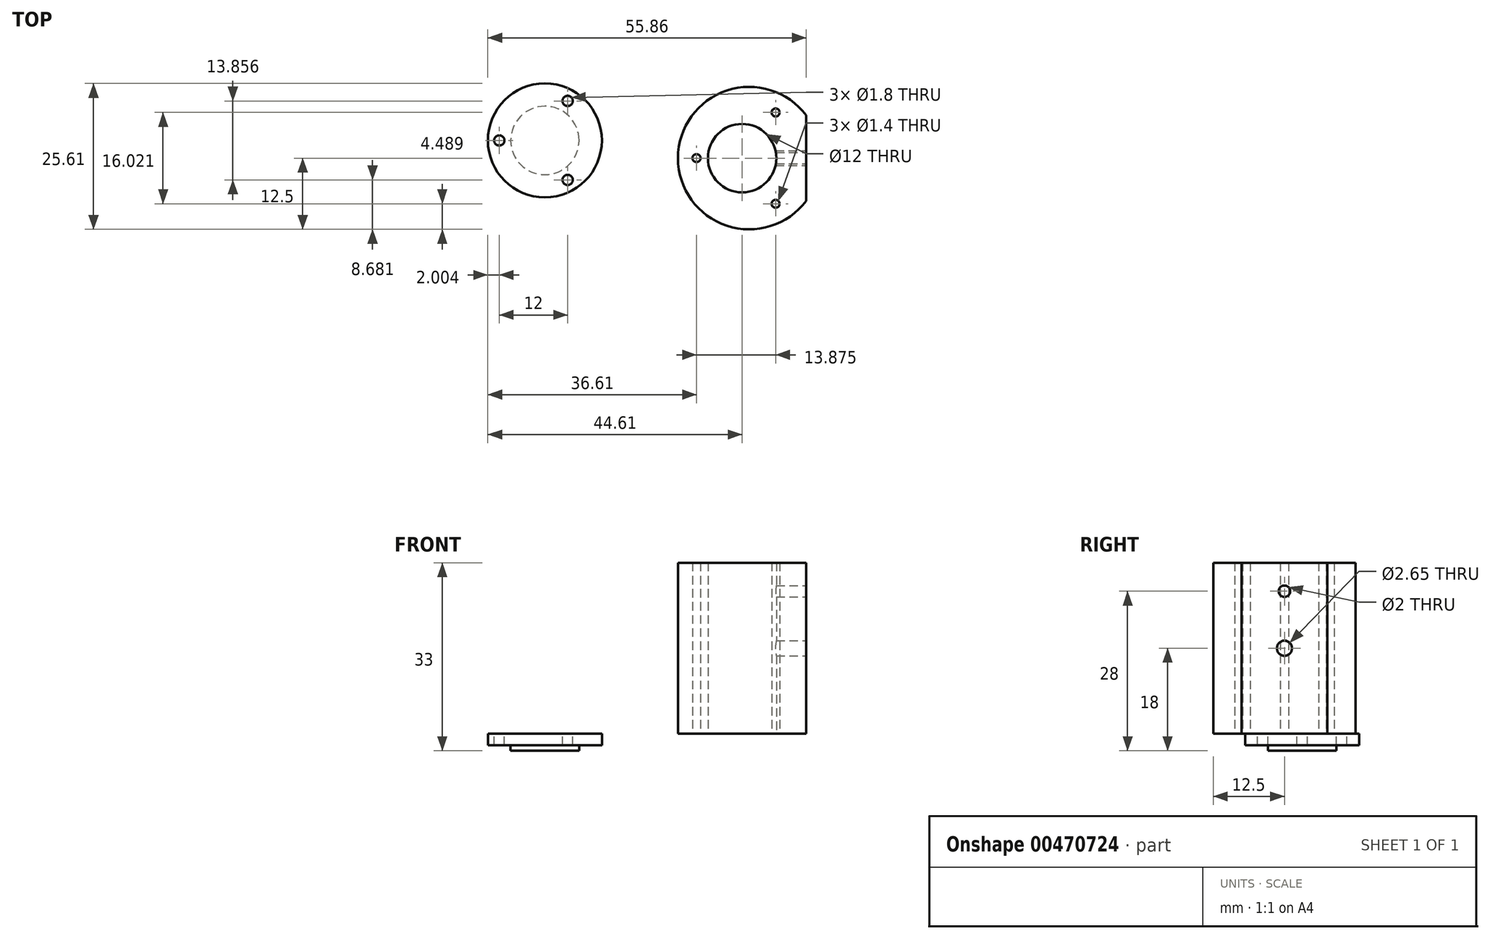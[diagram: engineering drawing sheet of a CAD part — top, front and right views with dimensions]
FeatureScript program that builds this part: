
annotation { "Feature Type Name" : "Feature", "Feature Type Description" : "" }
export const myFeature = defineFeature(function(context is Context, id is Id, definition is map)
    precondition{}
    {
        {
            var Q0;
            Q0=qCreatedBy(makeId("Top.planeOp"),FACE);
            var sketch = newSketch(context, id + "F0", { "sketchPlane" : qUnion([Q0])});
            skArc(sketch, "E0", {"start": v(10, 7.5) * mm, "mid": v(-12.5, 0) * mm, "end": v(10, -7.5) * mm});
            skLineSegment(sketch, "E1", {"start": v(10, 7.5) * mm, "end": v(10, -7.5) * mm});
            skPoint(sketch, "E2.start.orphan", {"position": v(12.5, 0) * mm});
            skLineSegment(sketch, "E3", {"start": v(10, 0) * mm, "end": v(-12.5, 0) * mm, "construction": true});
            skPoint(sketch, "E4", {"position": v(-1.25, 0) * mm});
            skCircle(sketch, "E5", {"center": v(-1.25, 0) * mm, "radius": 6 * mm});
            skLineSegment(sketch, "E6", {"start": v(-1.25, 0) * mm, "end": v(-9.25, 0) * mm, "construction": true});
            skPoint(sketch, "E7", {"position": v(-9.25, 0) * mm});
            skPoint(sketch, "E8.1.0", {"position": v(4.62, -8.01) * mm});
            skPoint(sketch, "E8.2.0", {"position": v(4.63, 8.01) * mm});
            skSolve(sketch);
        }
        {
            var Q0;
            Q0=makeQuery(id+"F0.imprint","IMPRINT",FACE,{"disambiguationData":[TD([[makeQuery(id+"F0.imprint","IMPRINT",EDGE,{"derivedFrom":sQuery(id+"F0.wireOp",EDGE,"E0")}),1.0]])]});
            extrude(context, id + "F1", {"entities" : qUnion([Q0]), "depth" : 30 * mm});
        }
        {
            var Q0;
            Q0=sQuery(id+"F0.wireOp",VERTEX,"E7");
            var Q1;
            Q1=sQuery(id+"F0.wireOp",VERTEX,"E8.2.0");
            var Q2;
            Q2=sQuery(id+"F0.wireOp",VERTEX,"E8.1.0");
            var Q3;
            Q3=makeQuery(id+"F1.opExtrude","SWEPT_BODY",BODY,{"disambiguationData":[OSD([sQuery(id+"F0.wireOp",EDGE,"E0"),sQuery(id+"F0.wireOp",EDGE,"E1"),sQuery(id+"F0.wireOp",EDGE,"E5")])]});
            hole(context, id + "F2", {"style" : HoleStyle.SIMPLE, "endStyle" : HoleEndStyle.THROUGH, "oppositeDirection" : true, "holeDiameter" : 1.4 * mm, "isTappedThrough" : true, "tappedDepth" : 12 * mm, "tapClearance" : 3, "startFromSketch" : true, "locations" : qUnion([Q0, Q1, Q2]), "scope" : qUnion([Q3])});
        }
        {
            var Q0;
            Q0=makeQuery(id+"F1.opExtrude","SWEPT_FACE",FACE,{"disambiguationData":[OSD([sQuery(id+"F0.wireOp",EDGE,"E1")])]});
            var sketch = newSketch(context, id + "F3", { "sketchPlane" : qUnion([Q0])});
            skLineSegment(sketch, "E9.0.0", {"start": v(-7.5, 0) * mm, "end": v(7.5, 0) * mm});
            skLineSegment(sketch, "E9.0.1", {"start": v(7.5, 0) * mm, "end": v(7.5, 30) * mm});
            skLineSegment(sketch, "E9.0.2", {"start": v(7.5, 30) * mm, "end": v(-7.5, 30) * mm});
            skLineSegment(sketch, "E9.0.3", {"start": v(-7.5, 30) * mm, "end": v(-7.5, 0) * mm});
            skPoint(sketch, "E10.0", {"position": v(0, 0) * mm});
            skLineSegment(sketch, "E11", {"start": v(0, 0) * mm, "end": v(0, 30) * mm, "construction": true});
            skPoint(sketch, "E12", {"position": v(0, 15) * mm});
            skPoint(sketch, "E13", {"position": v(0, 25) * mm});
            skSolve(sketch);
        }
        {
            var Q0;
            Q0=sQuery(id+"F3.wireOp",VERTEX,"E12");
            var Q1;
            Q1=makeQuery(id+"F1.opExtrude","SWEPT_BODY",BODY,{"disambiguationData":[OSD([sQuery(id+"F0.wireOp",EDGE,"E0"),sQuery(id+"F0.wireOp",EDGE,"E1"),sQuery(id+"F0.wireOp",EDGE,"E5")])]});
            hole(context, id + "F4", {"style" : HoleStyle.SIMPLE, "endStyle" : HoleEndStyle.BLIND, "holeDiameter" : 2.65 * mm, "holeDepth" : 10 * mm, "isTappedThrough" : true, "tappedDepth" : 12 * mm, "tapClearance" : 3, "startFromSketch" : true, "locations" : qUnion([Q0]), "scope" : qUnion([Q1])});
        }
        {
            var Q0;
            Q0=sQuery(id+"F3.wireOp",VERTEX,"E13");
            var Q1;
            Q1=makeQuery(id+"F1.opExtrude","SWEPT_BODY",BODY,{"disambiguationData":[OSD([sQuery(id+"F0.wireOp",EDGE,"E0"),sQuery(id+"F0.wireOp",EDGE,"E1"),sQuery(id+"F0.wireOp",EDGE,"E5")])]});
            hole(context, id + "F5", {"style" : HoleStyle.SIMPLE, "endStyle" : HoleEndStyle.BLIND, "holeDiameter" : 2 * mm, "holeDepth" : 10 * mm, "isTappedThrough" : true, "tappedDepth" : 12 * mm, "tapClearance" : 3, "startFromSketch" : true, "locations" : qUnion([Q0]), "scope" : qUnion([Q1])});
        }
        {
            var Q0;
            Q0=makeQuery(id+"F0.imprint","IMPRINT",FACE,{"disambiguationData":[TD([[makeQuery(id+"F0.imprint","IMPRINT",EDGE,{"derivedFrom":sQuery(id+"F0.wireOp",EDGE,"E0")}),1.0]])]});
            var sketch = newSketch(context, id + "F6", { "sketchPlane" : qUnion([Q0])});
            skCircle(sketch, "E14", {"center": v(-35.86, 3.1) * mm, "radius": 10 * mm});
            skLineSegment(sketch, "E15", {"start": v(-35.86, 3.1) * mm, "end": v(-43.86, 3.1) * mm, "construction": true});
            skPoint(sketch, "E16", {"position": v(-43.86, 3.1) * mm});
            skPoint(sketch, "E17.1.0", {"position": v(-31.86, -3.82) * mm});
            skPoint(sketch, "E17.2.0", {"position": v(-31.86, 10.04) * mm});
            skCircle(sketch, "E18", {"center": v(-35.86, 3.1) * mm, "radius": 6 * mm});
            skSolve(sketch);
        }
        {
            var Q0;
            Q0=makeQuery(id+"F6.imprint","IMPRINT",FACE,{"disambiguationData":[TD([[makeQuery(id+"F6.imprint","IMPRINT",EDGE,{"derivedFrom":sQuery(id+"F6.wireOp",EDGE,"E14")}),1.0]])]});
            extrude(context, id + "F7", {"entities" : qUnion([Q0]), "oppositeDirection" : true, "depth" : 2 * mm});
        }
        {
            var Q0;
            Q0=makeQuery(id+"F6.imprint","IMPRINT",FACE,{"disambiguationData":[TD([[makeQuery(id+"F6.imprint","IMPRINT",EDGE,{"derivedFrom":sQuery(id+"F6.wireOp",EDGE,"E18")}),1.0]])]});
            extrude(context, id + "F8", {"entities" : qUnion([Q0]), "operationType" : NewBodyOperationType.ADD, "oppositeDirection" : true, "depth" : 3 * mm});
        }
        {
            var Q0;
            Q0=sQuery(id+"F6.wireOp",VERTEX,"E17.2.0");
            var Q1;
            Q1=sQuery(id+"F6.wireOp",VERTEX,"E16");
            var Q2;
            Q2=sQuery(id+"F6.wireOp",VERTEX,"E17.1.0");
            var Q3;
            Q3=makeQuery(id+"F7.opExtrude","SWEPT_BODY",BODY,{"disambiguationData":[OSD([sQuery(id+"F6.wireOp",EDGE,"E14"),sQuery(id+"F6.wireOp",EDGE,"E18")])]});
            hole(context, id + "F9", {"style" : HoleStyle.SIMPLE, "endStyle" : HoleEndStyle.THROUGH, "holeDiameter" : 1.8 * mm, "isTappedThrough" : true, "tappedDepth" : 12 * mm, "tapClearance" : 3, "startFromSketch" : true, "locations" : qUnion([Q0, Q1, Q2]), "scope" : qUnion([Q3])});
        }
    });
